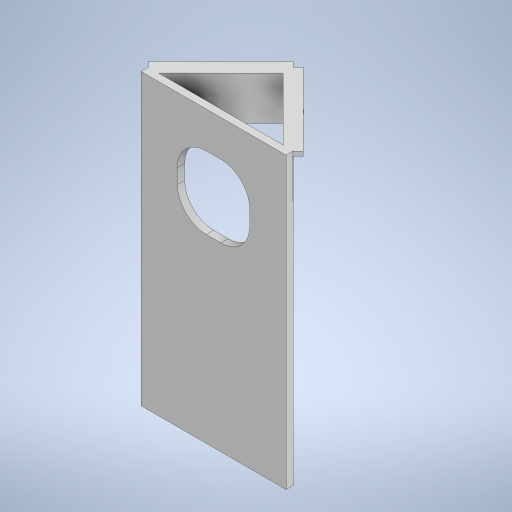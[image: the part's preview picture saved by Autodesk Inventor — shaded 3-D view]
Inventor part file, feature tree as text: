
AUTODESK INVENTOR PART (.ipt)
format: ipt  version: 2023 (Build 270158000, 158)  size: 290,816 bytes
history: native  units: mm
features: extrude x4, sketch x4
ambient origin geometry x8: Origin, YZ Plane, XZ Plane, XY Plane, X Axis, Y Axis, Z Axis, Center Point
bodies: Solid1 (feature_tree)
feature tree (8):
  extrude  "Extrusion1"  Depth=200.0mm
  extrude  "Extrusion2"  TaperAngle=45.0deg  [1 undecoded]
  extrude  "Extrusion6"  Depth=5.0mm
  extrude  "Extrusion9"  Depth=50.0mm
  sketch  "Sketch1"  dims[d0=100.0mm d1=200.0mm]
  sketch  "Sketch2"  dims[d2=5.0mm d3=0.0mm d4=45.0deg]
  sketch  "Sketch6"  dims[d5=5.0mm d6=5.0mm]
  sketch  "Sketch10"  dims[d7=30.0mm d8=0.0mm d21=50.0mm d22=50.0mm d23=20.0mm d24=5.0mm d25=0.0mm d33=5.0mm d34=5.0mm d36=3.0mm d37=0.0mm]
note: 1 required parameter value undecoded (feature->parameter linkage not recoverable at this tier; creation-order binding heuristic only, values carry confidence <= 0.55)
